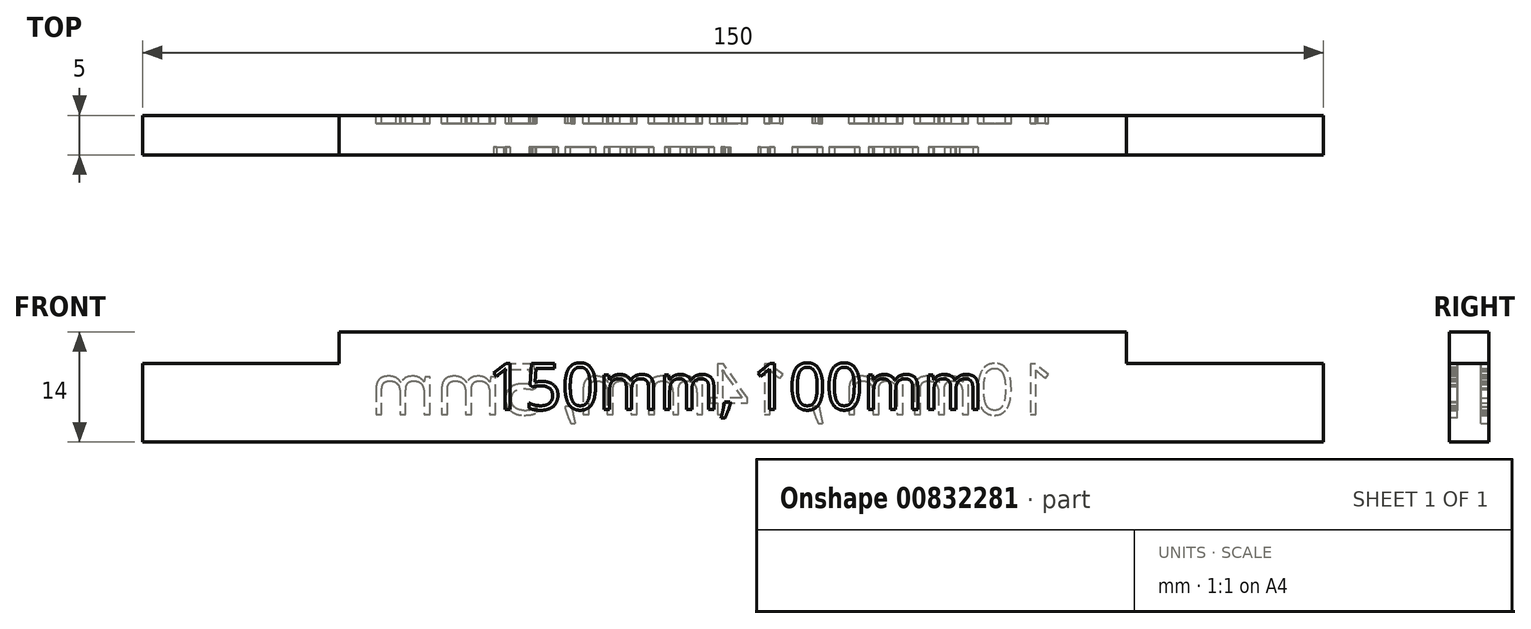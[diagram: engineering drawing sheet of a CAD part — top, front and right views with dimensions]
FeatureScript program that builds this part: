
annotation { "Feature Type Name" : "Feature", "Feature Type Description" : "" }
export const myFeature = defineFeature(function(context is Context, id is Id, definition is map)
    precondition{}
    {
        {
            var Q0;
            Q0=qCreatedBy(makeId("Top.planeOp"),FACE);
            var sketch = newSketch(context, id + "F0", { "sketchPlane" : qUnion([Q0])});
            skLineSegment(sketch, "E0.bottom", {"start": v(-75, 0) * mm, "end": v(75, 0) * mm});
            skLineSegment(sketch, "E0.top", {"start": v(-75, -5) * mm, "end": v(75, -5) * mm});
            skLineSegment(sketch, "E0.left", {"start": v(-75, 0) * mm, "end": v(-75, -5) * mm});
            skLineSegment(sketch, "E0.right", {"start": v(75, 0) * mm, "end": v(75, -5) * mm});
            skLineSegment(sketch, "E1", {"start": v(50, 0) * mm, "end": v(50, -5) * mm});
            skLineSegment(sketch, "E2", {"start": v(-50, 0) * mm, "end": v(-50, -5) * mm});
            skSolve(sketch);
        }
        {
            var Q0;
            Q0=makeQuery(id+"F0.imprint","IMPRINT",FACE,{"disambiguationData":[TD([[makeQuery(id+"F0.imprint","IMPRINT",EDGE,{"derivedFrom":sQuery(id+"F0.wireOp",EDGE,"E0.bottom")}),-1.0]])]});
            extrude(context, id + "F1", {"entities" : qUnion([Q0]), "depth" : 10 * mm, "offsetDistance" : 25 * mm});
        }
        {
            var Q0;
            {var subQ0=sQuery(id+"F0.wireOp",EDGE,"E1");Q0=makeQuery(id+"F0.imprint","IMPRINT",FACE,{"disambiguationData":[TD([[makeQuery(id+"F0.imprint","IMPRINT",EDGE,{"derivedFrom":subQ0}),-1.0]])]});}
            extrude(context, id + "F2", {"entities" : qUnion([Q0]), "operationType" : NewBodyOperationType.ADD, "depth" : 14 * mm, "offsetDistance" : 25 * mm});
        }
        {
            var Q0;
            {var subQ0=sQuery(id+"F0.wireOp",EDGE,"E0.top");Q0=makeQuery(id+"F2.boolean.opBoolean","MERGE",FACE,{"derivedFrom":[makeQuery(id+"F1.opExtrude","SWEPT_FACE",FACE,{"disambiguationData":[OSD([subQ0])]}),makeQuery(id+"F2.opExtrude","SWEPT_FACE",FACE,{"disambiguationData":[OSD([subQ0])]})]});}
            var sketch = newSketch(context, id + "F3", { "sketchPlane" : qUnion([Q0])});
            skText(sketch, "E3", { "text": "150mm, 100mm\n", "fontName": "OpenSans-Regular.ttf"});
            const initialGuessF3  = {"E3": [-0.03115, 0.00412, 1, 0, 0.00592]};
            skSetInitialGuess(sketch, initialGuessF3);
            skSolve(sketch);
        }
        {
            var Q0;
            Q0 = qSketchRegion(id + "F3", true);
            extrude(context, id + "F4", {"entities" : qUnion([Q0]), "operationType" : NewBodyOperationType.REMOVE, "oppositeDirection" : true, "depth" : 1 * mm, "offsetDistance" : 25 * mm});
        }
        {
            var Q0;
            {var subQ0=sQuery(id+"F0.wireOp",EDGE,"E0.bottom");Q0=makeQuery(id+"F2.boolean.opBoolean","MERGE",FACE,{"derivedFrom":[makeQuery(id+"F1.opExtrude","SWEPT_FACE",FACE,{"disambiguationData":[OSD([subQ0])]}),makeQuery(id+"F2.opExtrude","SWEPT_FACE",FACE,{"disambiguationData":[OSD([subQ0])]})]});}
            var sketch = newSketch(context, id + "F5", { "sketchPlane" : qUnion([Q0])});
            skText(sketch, "E4", { "text": "10mm , 14mm, 5mm", "fontName": "OpenSans-Regular.ttf"});
            const initialGuessF5  = {"E4": [-0.04092, 0.0035, 1, 0, 0.00645]};
            skSetInitialGuess(sketch, initialGuessF5);
            skSolve(sketch);
        }
        {
            var Q0;
            Q0 = qSketchRegion(id + "F5", true);
            extrude(context, id + "F6", {"entities" : qUnion([Q0]), "operationType" : NewBodyOperationType.REMOVE, "oppositeDirection" : true, "depth" : 1 * mm, "offsetDistance" : 25 * mm});
        }
    });
